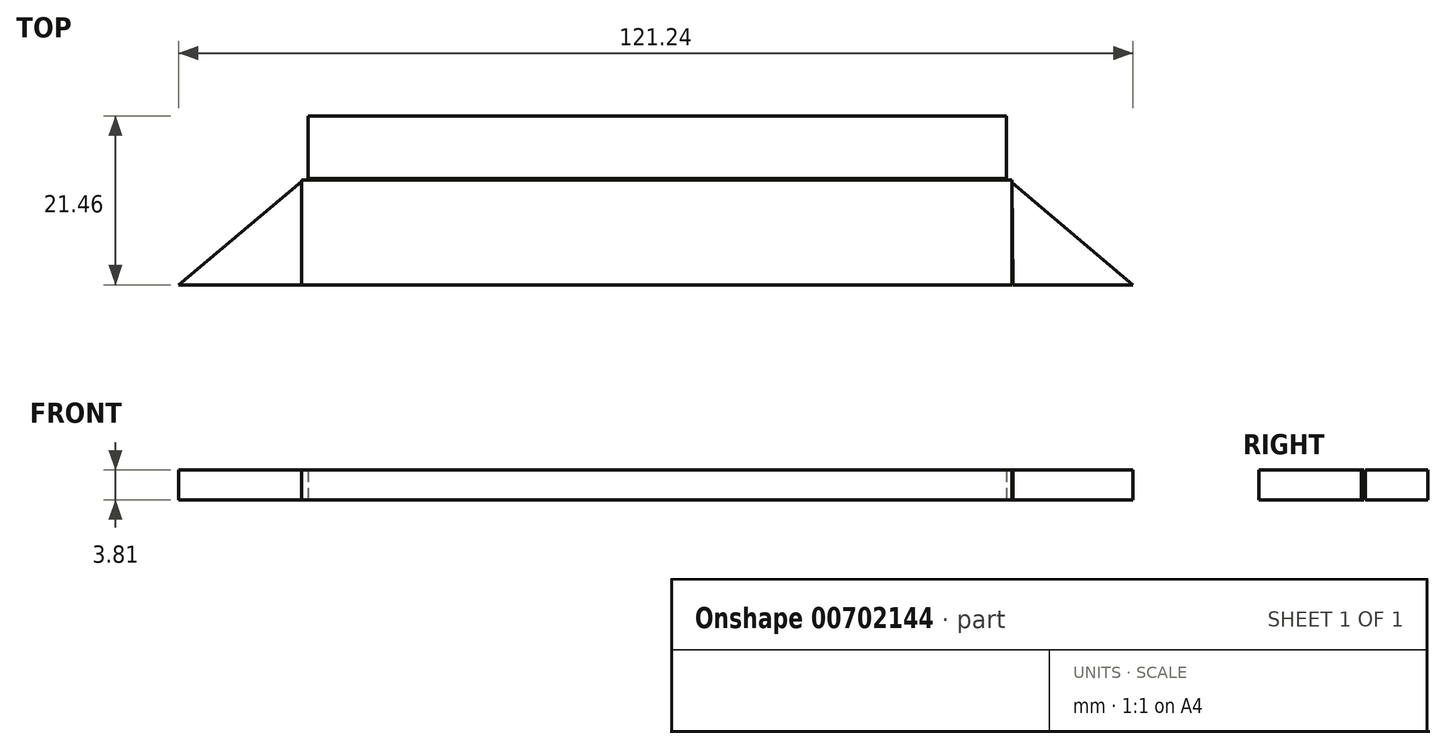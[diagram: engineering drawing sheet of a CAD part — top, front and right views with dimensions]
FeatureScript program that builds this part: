
annotation { "Feature Type Name" : "Feature", "Feature Type Description" : "" }
export const myFeature = defineFeature(function(context is Context, id is Id, definition is map)
    precondition{}
    {
        {
            var Q0;
            Q0=qCreatedBy(makeId("Top.planeOp"),FACE);
            var sketch = newSketch(context, id + "F0", { "sketchPlane" : qUnion([Q0])});
            skLineSegment(sketch, "E0.bottom", {"start": v(-46.73, 13.35) * mm, "end": v(43.49, 13.35) * mm});
            skLineSegment(sketch, "E0.top", {"start": v(-46.73, 0) * mm, "end": v(43.49, 0) * mm});
            skLineSegment(sketch, "E0.left", {"start": v(-46.73, 13.35) * mm, "end": v(-46.73, 0) * mm});
            skLineSegment(sketch, "E0.right", {"start": v(43.49, 13.35) * mm, "end": v(43.49, 0) * mm});
            skSolve(sketch);
        }
        {
            var Q0;
            Q0 = qSketchRegion(id + "F0", true);
            extrude(context, id + "F1", {"entities" : qUnion([Q0]), "depth" : 3.8 * mm, "offsetDistance" : 25.4 * mm});
        }
        {
            var Q0;
            Q0=qCreatedBy(makeId("Top.planeOp"),FACE);
            var sketch = newSketch(context, id + "F2", { "sketchPlane" : qUnion([Q0])});
            skLineSegment(sketch, "E1", {"start": v(-46.73, 13.16) * mm, "end": v(-62.37, 0) * mm});
            skLineSegment(sketch, "E2", {"start": v(-62.37, 0) * mm, "end": v(-46.73, 0) * mm});
            skLineSegment(sketch, "E3", {"start": v(-46.73, 0) * mm, "end": v(-46.73, 13.16) * mm});
            skSolve(sketch);
        }
        {
            var Q0;
            Q0=makeQuery(id+"F2.imprint","IMPRINT",FACE,{"disambiguationData":[TD([[makeQuery(id+"F2.imprint","IMPRINT",EDGE,{"derivedFrom":sQuery(id+"F2.wireOp",EDGE,"E1")}),1.0]])]});
            extrude(context, id + "F3", {"entities" : qUnion([Q0]), "depth" : 3.8 * mm, "offsetDistance" : 25.4 * mm});
        }
        {
            var Q0;
            Q0=qCreatedBy(makeId("Top.planeOp"),FACE);
            var sketch = newSketch(context, id + "F4", { "sketchPlane" : qUnion([Q0])});
            skLineSegment(sketch, "E4", {"start": v(43.49, 13.04) * mm, "end": v(58.87, 0) * mm});
            skLineSegment(sketch, "E5", {"start": v(58.87, 0) * mm, "end": v(43.65, 0) * mm});
            skLineSegment(sketch, "E6", {"start": v(43.65, 0) * mm, "end": v(43.49, 13.04) * mm});
            skSolve(sketch);
        }
        {
            var Q0;
            Q0 = qSketchRegion(id + "F4", true);
            extrude(context, id + "F5", {"entities" : qUnion([Q0]), "depth" : 3.8 * mm, "offsetDistance" : 25.4 * mm});
        }
        {
            var Q0;
            Q0=qCreatedBy(makeId("Top.planeOp"),FACE);
            var sketch = newSketch(context, id + "F6", { "sketchPlane" : qUnion([Q0])});
            skLineSegment(sketch, "E7.bottom", {"start": v(-45.92, 13.52) * mm, "end": v(42.84, 13.52) * mm});
            skLineSegment(sketch, "E7.top", {"start": v(-45.92, 21.46) * mm, "end": v(42.84, 21.46) * mm});
            skLineSegment(sketch, "E7.left", {"start": v(-45.92, 13.52) * mm, "end": v(-45.92, 21.46) * mm});
            skLineSegment(sketch, "E7.right", {"start": v(42.84, 13.52) * mm, "end": v(42.84, 21.46) * mm});
            skSolve(sketch);
        }
        {
            var Q0;
            Q0 = qSketchRegion(id + "F6", true);
            extrude(context, id + "F7", {"entities" : qUnion([Q0]), "depth" : 3.8 * mm, "offsetDistance" : 25.4 * mm});
        }
    });
